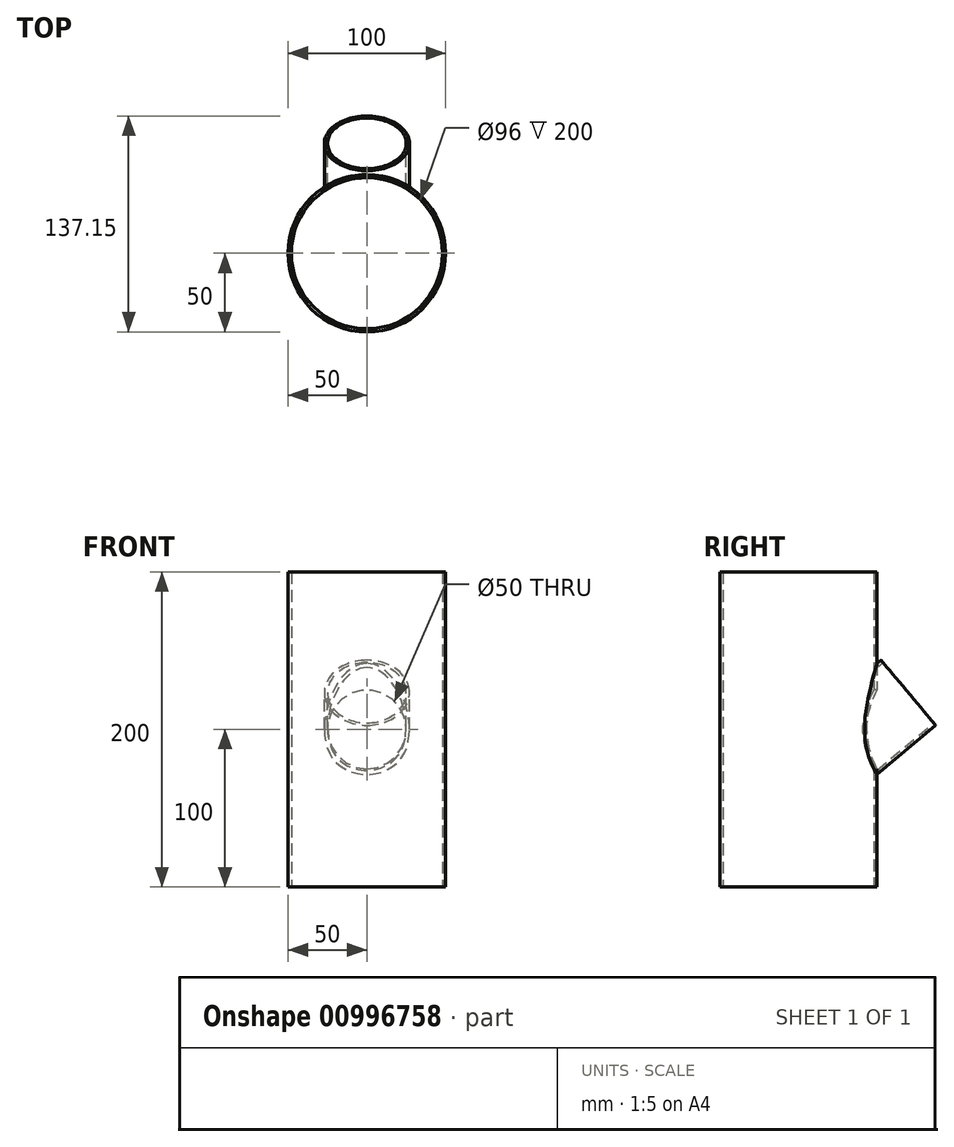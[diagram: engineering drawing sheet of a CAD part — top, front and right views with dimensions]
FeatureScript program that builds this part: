
annotation { "Feature Type Name" : "Feature", "Feature Type Description" : "" }
export const myFeature = defineFeature(function(context is Context, id is Id, definition is map)
    precondition{}
    {
        {
            var Q0;
            Q0=qCreatedBy(makeId("Top.planeOp"),FACE);
            var sketch = newSketch(context, id + "F0", { "sketchPlane" : qUnion([Q0])});
            skCircle(sketch, "E0", {"center": v(0, 0) * mm, "radius": 50 * mm});
            skCircle(sketch, "E1", {"center": v(0, 0) * mm, "radius": 48 * mm});
            skSolve(sketch);
        }
        {
            var Q0;
            Q0=makeQuery(id+"F0.imprint","IMPRINT",FACE,{"disambiguationData":[TD([[makeQuery(id+"F0.imprint","IMPRINT",EDGE,{"derivedFrom":sQuery(id+"F0.wireOp",EDGE,"E0")}),1.0]])]});
            extrude(context, id + "F1", {"entities" : qUnion([Q0]), "depth" : 100 * mm, "offsetDistance" : 25 * mm, "hasSecondDirection" : true, "secondDirectionOppositeDirection" : true, "secondDirectionDepth" : 100 * mm});
        }
        {
            var Q0;
            Q0=qCreatedBy(makeId("Front.planeOp"),FACE);
            var sketch = newSketch(context, id + "F2", { "sketchPlane" : qUnion([Q0])});
            skCircle(sketch, "E2", {"center": v(0, 0) * mm, "radius": 25 * mm});
            skSolve(sketch);
        }
        {
            var Q0;
            Q0 = qSketchRegion(id + "F2", true);
            var Q1;
            Q1=makeQuery(id+"F1.opExtrude","SWEPT_BODY",BODY,{"disambiguationData":[OSD([sQuery(id+"F0.wireOp",EDGE,"E0"),sQuery(id+"F0.wireOp",EDGE,"E1")])]});
            extrude(context, id + "F3", {"entities" : qUnion([Q0]), "operationType" : NewBodyOperationType.REMOVE, "oppositeDirection" : true, "depth" : 101 * mm, "offsetDistance" : 25 * mm, "hasSecondDirection" : true, "secondDirectionBound" : SecondDirectionBoundingType.UP_TO_BODY, "secondDirectionOppositeDirection" : false, "secondDirectionDepth" : 25 * mm, "secondDirectionBoundEntityBody" : qUnion([Q1])});
        }
        {
            var Q0;
            Q0=qCreatedBy(makeId("Front.planeOp"),FACE);
            cPlane(context, id + "F4", {"entities" : qUnion([Q0]), "cplaneType" : CPlaneType.OFFSET, "offset" : 60 * mm, "oppositeDirection" : true, "width" : 150 * mm, "height" : 150 * mm});
        }
        {
            var Q0;
            Q0=qCreatedBy(id+"F4.planeOp",FACE);
            var sketch = newSketch(context, id + "F5", { "sketchPlane" : qUnion([Q0])});
            skLineSegment(sketch, "E3", {"start": v(34.03, 35) * mm, "end": v(-35.97, 35) * mm});
            skSolve(sketch);
        }
        {
            var Q0;
            Q0=sQuery(id+"F5.wireOp",EDGE,"E3");
            cPlane(context, id + "F6", {"entities" : qUnion([Q0]), "cplaneType" : CPlaneType.LINE_ANGLE, "offset" : 25 * mm, "angle" : 40 * degree, "oppositeDirection" : true, "width" : 150 * mm, "height" : 150 * mm});
        }
        {
            var Q0;
            Q0=qCreatedBy(id+"F6.planeOp",FACE);
            var sketch = newSketch(context, id + "F7", { "sketchPlane" : qUnion([Q0])});
            skFitSpline(sketch, "E4.0", {"points": [v(-1.26, -51.27) * mm, v(0, -51.3) * mm, v(1.26, -51.27) * mm, v(2.91, -51.13) * mm, v(4.55, -50.86) * mm, v(6.15, -50.47) * mm, v(7.35, -50.1) * mm, v(8.53, -49.68) * mm, v(10.06, -49.04) * mm, v(11.9, -48.1) * mm, v(13.63, -47) * mm, v(14.96, -46.02) * mm, v(16.23, -45) * mm, v(17.71, -43.62) * mm, v(19.06, -42.14) * mm, v(20.06, -40.89) * mm, v(21, -39.6) * mm, v(22.03, -37.96) * mm, v(23.08, -35.95) * mm, v(23.78, -34.24) * mm, v(24.23, -32.85) * mm, v(24.6, -31.49) * mm, v(24.91, -29.81) * mm, v(25.02, -28.2) * mm, v(24.98, -26.93) * mm, v(24.86, -25.69) * mm, v(24.55, -24.23) * mm, v(24.05, -22.88) * mm, v(23.53, -21.87) * mm, v(22.93, -20.9) * mm, v(22.06, -19.77) * mm, v(21.02, -18.76) * mm, v(20.09, -18.02) * mm, v(19.09, -17.31) * mm, v(17.74, -16.52) * mm, v(15.97, -15.69) * mm, v(14.35, -15.09) * mm, v(12.97, -14.66) * mm, v(11.56, -14.28) * mm, v(10.1, -13.95) * mm, v(8.59, -13.67) * mm, v(7.42, -13.5) * mm, v(6.23, -13.34) * mm, v(4.6, -13.17) * mm, v(2.55, -13.03) * mm, v(0.49, -12.98) * mm, v(-1.18, -13) * mm, v(-2.43, -13.04) * mm, v(-3.68, -13.1) * mm, v(-5.31, -13.23) * mm, v(-6.9, -13.41) * mm, v(-8.47, -13.65) * mm, v(-9.62, -13.86) * mm, v(-10.76, -14.1) * mm, v(-12.21, -14.44) * mm, v(-13.95, -14.94) * mm, v(-15.57, -15.54) * mm, v(-16.8, -16.08) * mm, v(-17.97, -16.66) * mm, v(-19.31, -17.44) * mm, v(-20.52, -18.34) * mm, v(-21.4, -19.12) * mm, v(-22.2, -19.96) * mm, v(-23.08, -21.07) * mm, v(-23.91, -22.54) * mm, v(-24.43, -23.88) * mm, v(-24.72, -25.04) * mm, v(-24.93, -26.23) * mm, v(-25.04, -27.77) * mm, v(-24.92, -29.72) * mm, v(-24.55, -31.76) * mm, v(-23.95, -33.82) * mm, v(-23.12, -35.87) * mm, v(-22.06, -37.93) * mm, v(-20.8, -39.9) * mm, v(-19.6, -41.48) * mm, v(-18.55, -42.7) * mm, v(-17.43, -43.88) * mm, v(-15.95, -45.26) * mm, v(-14.34, -46.5) * mm, v(-12.97, -47.42) * mm, v(-11.91, -48.06) * mm, v(-10.81, -48.66) * mm, v(-9.32, -49.37) * mm, v(-7.4, -50.12) * mm, v(-5.4, -50.67) * mm, v(-3.77, -51) * mm, v(-2.52, -51.16) * mm, v(-1.26, -51.27) * mm, v(0, -51.3) * mm, v(1.26, -51.27) * mm, v(-1.26, -51.27) * mm], "construction": true});
            skLineSegment(sketch, "E5", {"start": v(0, 0) * mm, "end": v(0, -27) * mm, "construction": true});
            skCircle(sketch, "E6", {"center": v(0, -27) * mm, "radius": 25 * mm});
            skCircle(sketch, "E7.0", {"center": v(0, -27) * mm, "radius": 27 * mm});
            skPoint(sketch, "E8.0", {"position": v(0, 0) * mm});
            skSolve(sketch);
        }
        {
            var Q0;
            Q0=makeQuery(id+"F7.imprint","IMPRINT",FACE,{"disambiguationData":[TD([[makeQuery(id+"F7.imprint","IMPRINT",EDGE,{"derivedFrom":sQuery(id+"F7.wireOp",EDGE,"E6")}),-1.0]])]});
            var Q1;
            Q1=makeQuery(id+"F1.opExtrude","SWEPT_FACE",FACE,{"disambiguationData":[OSD([sQuery(id+"F0.wireOp",EDGE,"E0")])]});
            extrude(context, id + "F8", {"entities" : qUnion([Q0]), "endBound" : BoundingType.UP_TO_SURFACE, "depth" : 25 * mm, "endBoundEntityFace" : qUnion([Q1]), "offsetDistance" : 25 * mm});
        }
        {
            var Q0;
            Q0=qCreatedBy(makeId("Right.planeOp"),FACE);
            var sketch = newSketch(context, id + "F9", { "sketchPlane" : qUnion([Q0])});
            skLineSegment(sketch, "E9", {"start": v(91, 7.12) * mm, "end": v(46.27, -17.36) * mm});
            skLineSegment(sketch, "E10", {"start": v(46.27, -17.36) * mm, "end": v(35.02, -3.95) * mm});
            skLineSegment(sketch, "E11", {"start": v(35.02, -3.95) * mm, "end": v(73.32, 28.19) * mm, "construction": true});
            skLineSegment(sketch, "E12", {"start": v(73.32, 28.19) * mm, "end": v(91, 7.12) * mm, "construction": true});
            skLineSegment(sketch, "E13", {"start": v(48, 100) * mm, "end": v(48, -100) * mm, "construction": true});
            skLineSegment(sketch, "E14", {"start": v(48, -57.62) * mm, "end": v(99.06, -57.62) * mm, "construction": true});
            skSolve(sketch);
        }
        {
            var Q0;
            Q0=sQuery(id+"F9.wireOp",EDGE,"E9");
            var Q1;
            Q1=sQuery(id+"F9.wireOp",EDGE,"E10");
            var Q2;
            Q2=sQuery(id+"F9.wireOp",EDGE,"E11");
            revolve(context, id + "F10", {"bodyType" : ToolBodyType.SURFACE, "surfaceOperationType" : NewSurfaceOperationType.NEW, "surfaceEntities" : qUnion([Q0, Q1]), "axis" : qUnion([Q2]), "revolveType" : RevolveType.FULL});
        }
    });
